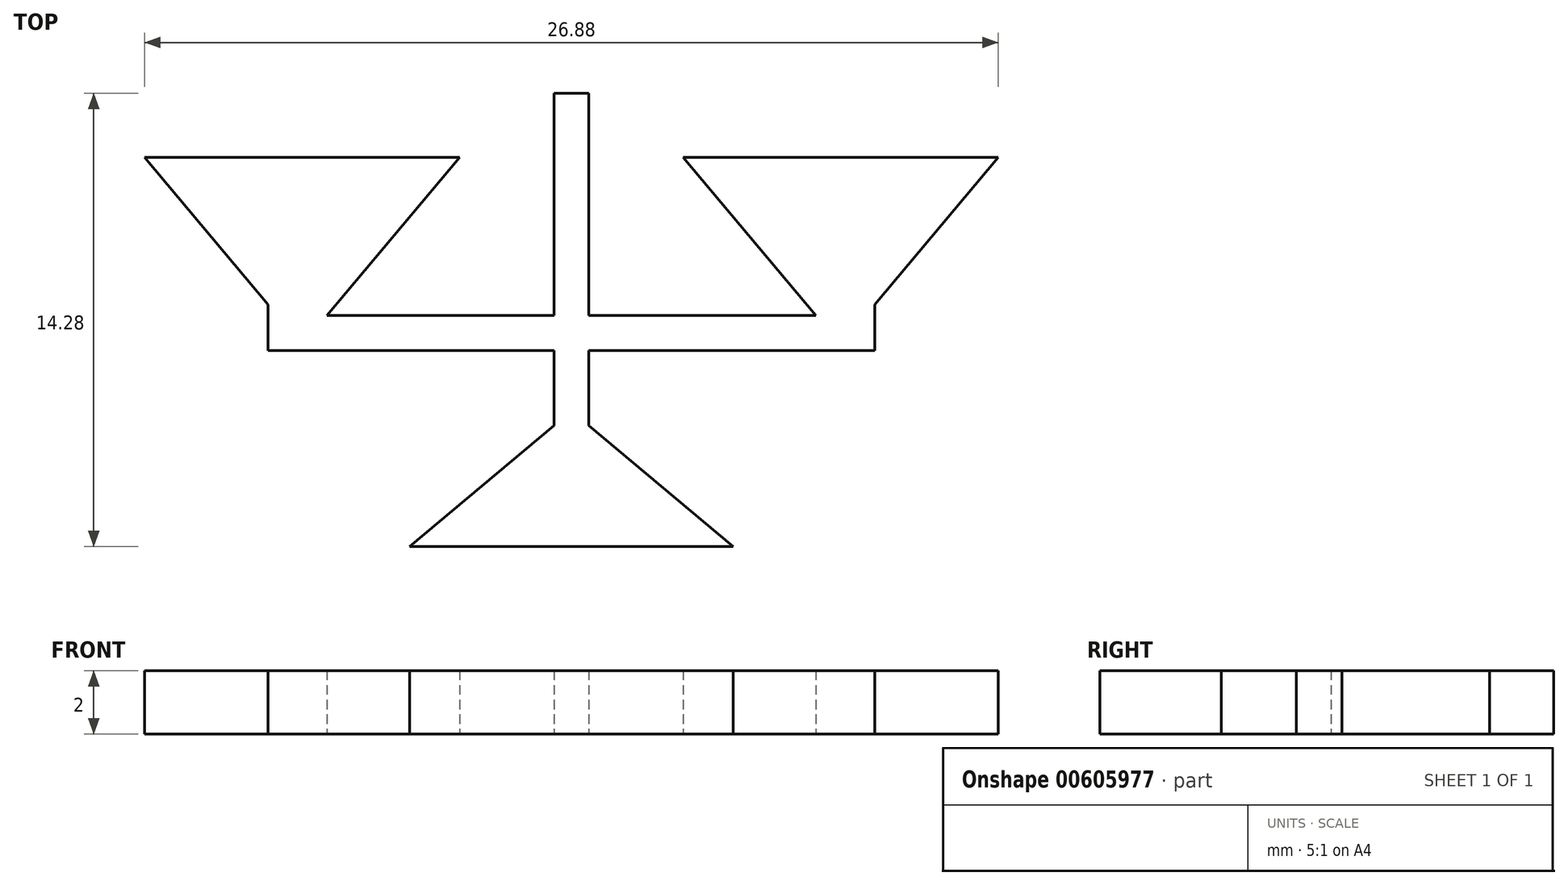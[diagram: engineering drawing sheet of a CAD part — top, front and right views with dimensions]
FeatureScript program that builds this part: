
annotation { "Feature Type Name" : "Feature", "Feature Type Description" : "" }
export const myFeature = defineFeature(function(context is Context, id is Id, definition is map)
    precondition{}
    {
        {
            var Q0;
            Q0=qCreatedBy(makeId("Top.planeOp"),FACE);
            var sketch = newSketch(context, id + "F0", { "sketchPlane" : qUnion([Q0])});
            skLineSegment(sketch, "E0", {"start": v(0, -11.75) * mm, "end": v(0, 20.53) * mm, "construction": true});
            skLineSegment(sketch, "E1", {"start": v(0, 7) * mm, "end": v(0.8, 7) * mm});
            skLineSegment(sketch, "E2", {"start": v(0.8, 7) * mm, "end": v(0.8, 0) * mm});
            skLineSegment(sketch, "E3", {"start": v(0.8, 0) * mm, "end": v(7.16, 0) * mm});
            skLineSegment(sketch, "E4", {"start": v(7.16, 0) * mm, "end": v(2.98, 4.98) * mm});
            skLineSegment(sketch, "E5", {"start": v(2.98, 4.98) * mm, "end": v(13.98, 4.98) * mm});
            skLineSegment(sketch, "E6", {"start": v(13.98, 4.98) * mm, "end": v(9.8, 0) * mm});
            skLineSegment(sketch, "E7", {"start": v(9.8, 0) * mm, "end": v(9.8, -1.6) * mm});
            skLineSegment(sketch, "E8", {"start": v(9.8, -1.6) * mm, "end": v(0.8, -1.6) * mm});
            skLineSegment(sketch, "E9", {"start": v(0.8, -1.6) * mm, "end": v(0.8, -3.6) * mm});
            skLineSegment(sketch, "E10", {"start": v(0.8, -3.6) * mm, "end": v(5.78, -7.78) * mm});
            skLineSegment(sketch, "E11", {"start": v(5.78, -7.78) * mm, "end": v(0, -7.78) * mm});
            skLineSegment(sketch, "E12", {"start": v(8.48, 4.98) * mm, "end": v(8.48, 0) * mm, "construction": true});
            skLineSegment(sketch, "E13.MirrorCS", {"start": v(0, 7) * mm, "end": v(-0.8, 7) * mm});
            skLineSegment(sketch, "E14.MirrorCS", {"start": v(-9.8, 0) * mm, "end": v(-9.8, -1.6) * mm});
            skLineSegment(sketch, "E15.MirrorCS", {"start": v(-0.8, 7) * mm, "end": v(-0.8, 0) * mm});
            skLineSegment(sketch, "E16.MirrorCS", {"start": v(-0.8, 0) * mm, "end": v(-7.16, 0) * mm});
            skLineSegment(sketch, "E17.MirrorCS", {"start": v(-7.16, 0) * mm, "end": v(-2.98, 4.98) * mm});
            skLineSegment(sketch, "E18.MirrorCS", {"start": v(-2.98, 4.98) * mm, "end": v(-13.98, 4.98) * mm});
            skLineSegment(sketch, "E19.MirrorCS", {"start": v(-13.98, 4.98) * mm, "end": v(-9.8, 0) * mm});
            skLineSegment(sketch, "E20.MirrorCS", {"start": v(-9.8, -1.6) * mm, "end": v(-0.8, -1.6) * mm});
            skLineSegment(sketch, "E21.MirrorCS", {"start": v(-0.8, -1.6) * mm, "end": v(-0.8, -3.6) * mm});
            skLineSegment(sketch, "E22.MirrorCS", {"start": v(-0.8, -3.6) * mm, "end": v(-5.78, -7.78) * mm});
            skLineSegment(sketch, "E23.MirrorCS", {"start": v(-5.78, -7.78) * mm, "end": v(0, -7.78) * mm});
            skLineSegment(sketch, "E24.0", {"start": v(-9.55, -1.35) * mm, "end": v(-0.55, -1.35) * mm});
            skLineSegment(sketch, "E24.1", {"start": v(-9.55, 0.1) * mm, "end": v(-9.55, -1.35) * mm});
            skLineSegment(sketch, "E24.2", {"start": v(-13.44, 4.73) * mm, "end": v(-9.55, 0.1) * mm});
            skLineSegment(sketch, "E24.3", {"start": v(-3.51, 4.73) * mm, "end": v(-13.44, 4.73) * mm});
            skLineSegment(sketch, "E24.4", {"start": v(-7.7, -0.25) * mm, "end": v(-3.51, 4.73) * mm});
            skLineSegment(sketch, "E24.5", {"start": v(-0.55, -1.35) * mm, "end": v(-0.55, -3.72) * mm});
            skLineSegment(sketch, "E24.6", {"start": v(-0.55, -0.25) * mm, "end": v(-7.7, -0.25) * mm});
            skLineSegment(sketch, "E24.7", {"start": v(-0.55, 6.75) * mm, "end": v(-0.55, -0.25) * mm});
            skLineSegment(sketch, "E24.8", {"start": v(0, 6.75) * mm, "end": v(-0.55, 6.75) * mm});
            skLineSegment(sketch, "E24.9", {"start": v(0, 6.75) * mm, "end": v(0.55, 6.75) * mm});
            skLineSegment(sketch, "E24.10", {"start": v(0.55, 6.75) * mm, "end": v(0.55, -0.25) * mm});
            skLineSegment(sketch, "E24.11", {"start": v(0.55, -0.25) * mm, "end": v(7.7, -0.25) * mm});
            skLineSegment(sketch, "E24.12", {"start": v(0.55, -3.72) * mm, "end": v(5.1, -7.53) * mm});
            skLineSegment(sketch, "E24.13", {"start": v(5.1, -7.53) * mm, "end": v(0, -7.53) * mm});
            skLineSegment(sketch, "E24.14", {"start": v(-5.1, -7.53) * mm, "end": v(0, -7.53) * mm});
            skLineSegment(sketch, "E24.15", {"start": v(-0.55, -3.72) * mm, "end": v(-5.1, -7.53) * mm});
            skLineSegment(sketch, "E24.16", {"start": v(0.55, -1.35) * mm, "end": v(0.55, -3.72) * mm});
            skLineSegment(sketch, "E24.17", {"start": v(9.55, -1.35) * mm, "end": v(0.55, -1.35) * mm});
            skLineSegment(sketch, "E24.18", {"start": v(9.55, 0.1) * mm, "end": v(9.55, -1.35) * mm});
            skLineSegment(sketch, "E24.19", {"start": v(13.44, 4.73) * mm, "end": v(9.55, 0.1) * mm});
            skLineSegment(sketch, "E24.20", {"start": v(3.51, 4.73) * mm, "end": v(13.44, 4.73) * mm});
            skLineSegment(sketch, "E24.21", {"start": v(7.7, -0.25) * mm, "end": v(3.51, 4.73) * mm});
            skSolve(sketch);
        }
        {
            var Q0;
            Q0=makeQuery(id+"F0.imprint","IMPRINT",FACE,{"disambiguationData":[TD([[makeQuery(id+"F0.imprint","IMPRINT",EDGE,{"derivedFrom":sQuery(id+"F0.wireOp",EDGE,"E24.0")}),1.0]])]});
            extrude(context, id + "F1", {"entities" : qUnion([Q0]), "depth" : 2 * mm});
        }
    });
